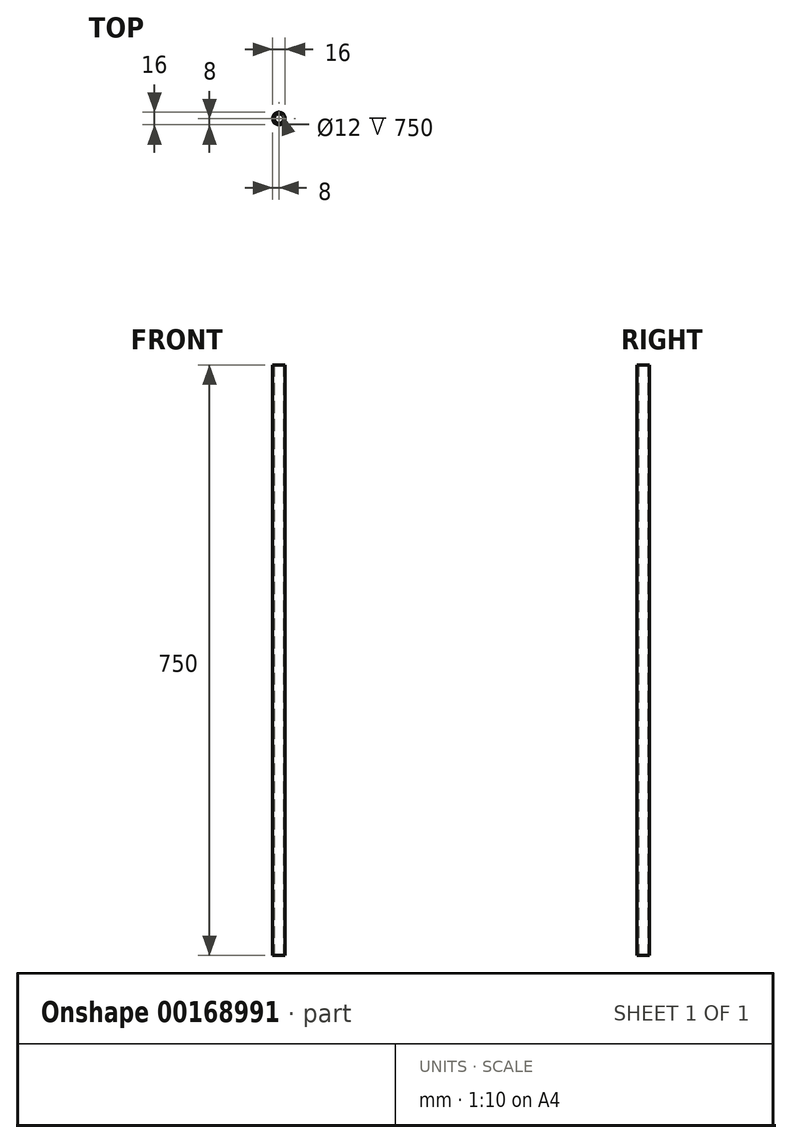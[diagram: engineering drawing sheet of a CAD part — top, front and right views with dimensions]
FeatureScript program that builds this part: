
annotation { "Feature Type Name" : "Feature", "Feature Type Description" : "" }
export const myFeature = defineFeature(function(context is Context, id is Id, definition is map)
    precondition{}
    {
        {
            var Q0;
            Q0=qCreatedBy(makeId("Top.planeOp"),FACE);
            var sketch = newSketch(context, id + "F0", { "sketchPlane" : qUnion([Q0])});
            skCircle(sketch, "E0", {"center": v(0, 0) * mm, "radius": 6 * mm});
            skCircle(sketch, "E1", {"center": v(0, 0) * mm, "radius": 8 * mm});
            skSolve(sketch);
        }
        {
            var Q0;
            Q0=makeQuery(id+"F0.imprint","IMPRINT",FACE,{"disambiguationData":[TD([[makeQuery(id+"F0.imprint","IMPRINT",EDGE,{"derivedFrom":sQuery(id+"F0.wireOp",EDGE,"E0")}),-1.0]])]});
            extrude(context, id + "F1", {"entities" : qUnion([Q0]), "depth" : 750 * mm});
        }
    });
